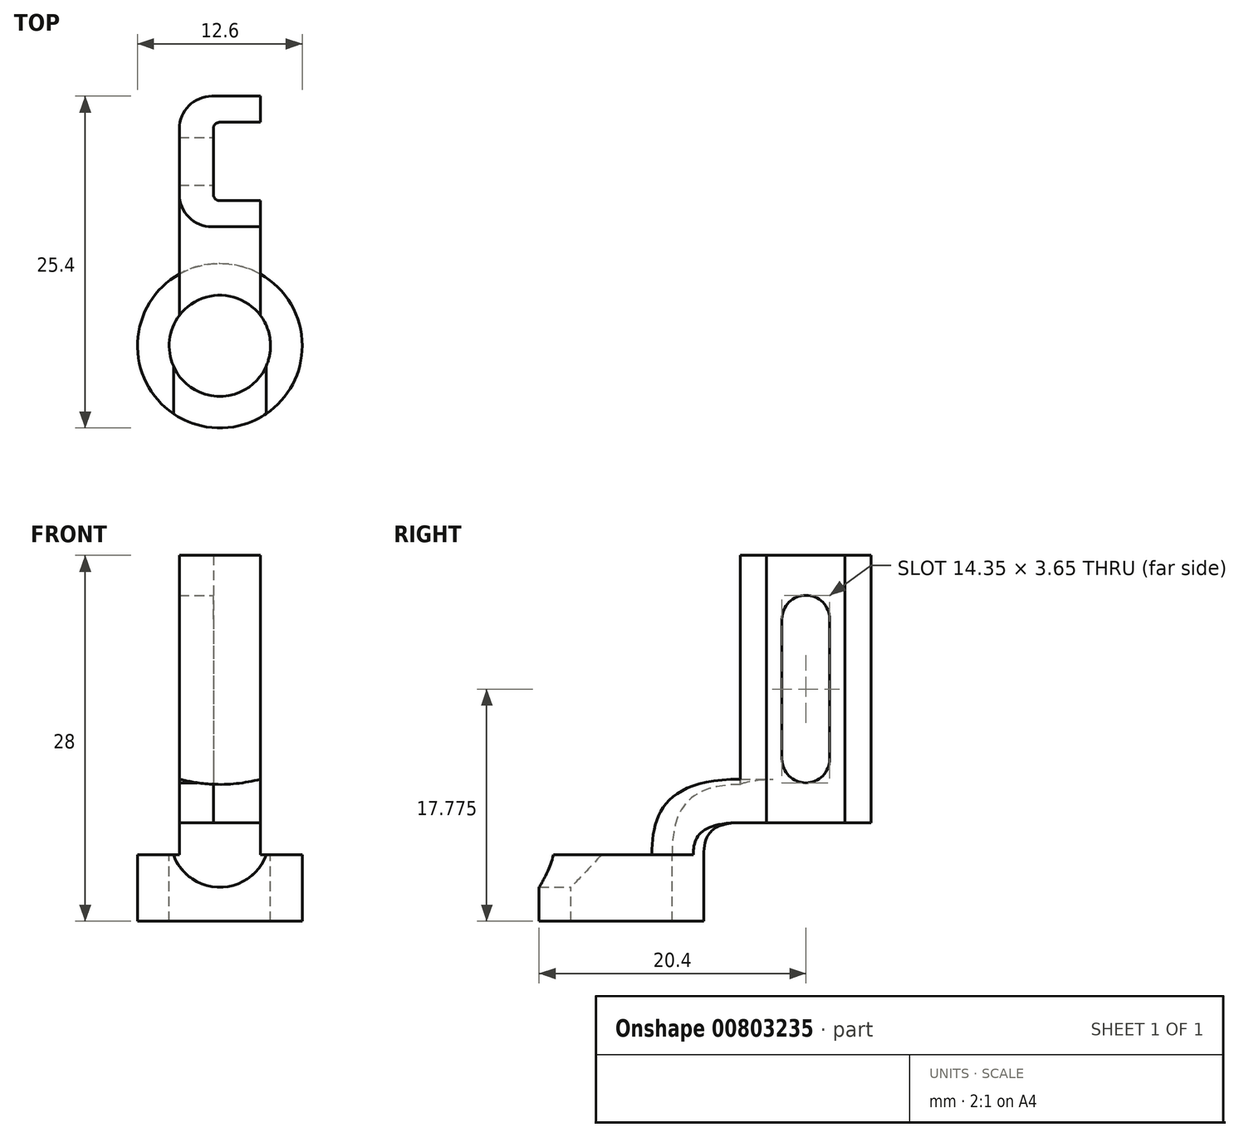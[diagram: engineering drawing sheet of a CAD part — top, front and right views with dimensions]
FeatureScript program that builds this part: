
annotation { "Feature Type Name" : "Feature", "Feature Type Description" : "" }
export const myFeature = defineFeature(function(context is Context, id is Id, definition is map)
    precondition{}
    {
        {
            var Q0;
            Q0=qCreatedBy(makeId("Top.planeOp"),FACE);
            var sketch = newSketch(context, id + "F0", { "sketchPlane" : qUnion([Q0])});
            skCircle(sketch, "E0", {"center": v(0, 0) * mm, "radius": 3.88 * mm});
            skCircle(sketch, "E1", {"center": v(0, 0) * mm, "radius": 6.3 * mm});
            skSolve(sketch);
        }
        {
            var Q0;
            Q0 = qSketchRegion(id + "F0", true);
            extrude(context, id + "F1", {"entities" : qUnion([Q0]), "oppositeDirection" : true, "depth" : 5.1 * mm, "offsetDistance" : 25 * mm});
        }
        {
            var Q0;
            Q0=makeQuery(id+"F1.opExtrude","CAP_FACE",FACE,{"disambiguationData":[OSD([sQuery(id+"F0.wireOp",EDGE,"E0"),sQuery(id+"F0.wireOp",EDGE,"E1")])],"isStart":true});
            cPlane(context, id + "F2", {"entities" : qUnion([Q0]), "cplaneType" : CPlaneType.OFFSET, "offset" : (7.55 - 5.1) * mm, "width" : 150 * mm, "height" : 150 * mm});
        }
        {
            var Q0;
            Q0=qCreatedBy(id+"F2.planeOp",FACE);
            var sketch = newSketch(context, id + "F3", { "sketchPlane" : qUnion([Q0])});
            skLineSegment(sketch, "E2.bottom", {"start": v(-3.1, 9.1) * mm, "end": v(3.1, 9.1) * mm});
            skLineSegment(sketch, "E2.top", {"start": v(-3.1, 19.1) * mm, "end": v(3.1, 19.1) * mm});
            skLineSegment(sketch, "E2.left", {"start": v(-3.1, 9.1) * mm, "end": v(-3.1, 19.1) * mm});
            skLineSegment(sketch, "E2.right", {"start": v(3.1, 9.1) * mm, "end": v(3.1, 11.1) * mm});
            skLineSegment(sketch, "E3", {"start": v(-3.1, 14.1) * mm, "end": v(3.1, 14.1) * mm, "construction": true});
            skLineSegment(sketch, "E4", {"start": v(3.1, 17.1) * mm, "end": v(-0.5, 17.1) * mm});
            skLineSegment(sketch, "E5", {"start": v(-0.5, 17.1) * mm, "end": v(-0.5, 14.1) * mm});
            skLineSegment(sketch, "E6.MirrorCS", {"start": v(3.1, 11.1) * mm, "end": v(-0.5, 11.1) * mm});
            skLineSegment(sketch, "E7.MirrorCS", {"start": v(-0.5, 11.1) * mm, "end": v(-0.5, 14.1) * mm});
            skLineSegment(sketch, "E8.trimOffspring", {"start": v(3.1, 17.1) * mm, "end": v(3.1, 19.1) * mm});
            skSolve(sketch);
        }
        {
            var Q0;
            Q0 = qSketchRegion(id + "F3", true);
            extrude(context, id + "F4", {"entities" : qUnion([Q0]), "depth" : 20.45 * mm, "offsetDistance" : 25 * mm});
        }
        {
            var Q0;
            Q0=makeQuery(id+"F4.opExtrude","SWEPT_FACE",FACE,{"disambiguationData":[OSD([sQuery(id+"F3.wireOp",EDGE,"E5"),sQuery(id+"F3.wireOp",EDGE,"E7.MirrorCS")])]});
            var sketch = newSketch(context, id + "F5", { "sketchPlane" : qUnion([Q0])});
            skLineSegment(sketch, "E9", {"start": v(11.1, 12.67) * mm, "end": v(17.1, 12.67) * mm, "construction": true});
            skLineSegment(sketch, "E10", {"start": v(14.1, 22.9) * mm, "end": v(14.1, 2.45) * mm, "construction": true});
            skArc(sketch, "E11", {"start": v(15.92, 18.02) * mm, "mid": v(14.1, 19.85) * mm, "end": v(12.27, 18.02) * mm});
            skLineSegment(sketch, "E12", {"start": v(12.27, 18.02) * mm, "end": v(12.27, 12.67) * mm});
            skLineSegment(sketch, "E13", {"start": v(15.92, 18.02) * mm, "end": v(15.92, 12.67) * mm});
            skLineSegment(sketch, "E14.MirrorCS", {"start": v(15.92, 7.32) * mm, "end": v(15.92, 12.67) * mm});
            skArc(sketch, "E15.MirrorCS", {"start": v(15.92, 7.32) * mm, "mid": v(14.1, 5.5) * mm, "end": v(12.27, 7.32) * mm});
            skLineSegment(sketch, "E16.MirrorCS", {"start": v(12.27, 7.32) * mm, "end": v(12.27, 12.67) * mm});
            skSolve(sketch);
        }
        {
            var Q0;
            Q0 = qSketchRegion(id + "F5", true);
            extrude(context, id + "F6", {"entities" : qUnion([Q0]), "operationType" : NewBodyOperationType.REMOVE, "endBound" : BoundingType.UP_TO_NEXT, "oppositeDirection" : true, "depth" : 25 * mm, "offsetDistance" : 25 * mm});
        }
        {
            var Q0;
            Q0=makeQuery(id+"F4.opExtrude","SWEPT_FACE",FACE,{"disambiguationData":[OSD([sQuery(id+"F3.wireOp",EDGE,"E2.bottom")])]});
            var sketch = newSketch(context, id + "F7", { "sketchPlane" : qUnion([Q0])});
            skLineSegment(sketch, "E17.bottom", {"start": v(3.1, 5.78) * mm, "end": v(-3.1, 5.78) * mm});
            skLineSegment(sketch, "E17.left", {"start": v(3.1, -6.22) * mm, "end": v(3.1, 5.78) * mm});
            skLineSegment(sketch, "E17.right", {"start": v(-3.1, -6.22) * mm, "end": v(-3.1, 5.78) * mm});
            skPoint(sketch, "E18.centerSnap0", {"position": v(0, -6.22) * mm});
            skLineSegment(sketch, "E19", {"start": v(-3.1, -6.22) * mm, "end": v(3.1, -6.22) * mm});
            skSolve(sketch);
        }
        {
            var Q0;
            Q0=makeQuery(id+"F1.opExtrude","CAP_FACE",FACE,{"disambiguationData":[OSD([sQuery(id+"F0.wireOp",EDGE,"E0"),sQuery(id+"F0.wireOp",EDGE,"E1")])],"isStart":true});
            var sketch = newSketch(context, id + "F8", { "sketchPlane" : qUnion([Q0])});
            skCircle(sketch, "E20.0", {"center": v(0, 0) * mm, "radius": 3.88 * mm});
            skSolve(sketch);
        }
        {
            var Q0;
            {var subQ0=sQuery(id+"F7.wireOp",EDGE,"E17.bottom");Q0=makeQuery(id+"F7.imprint","IMPRINT",FACE,{"disambiguationData":[TD([[makeQuery(id+"F7.imprint","IMPRINT",EDGE,{"derivedFrom":subQ0}),-1.0]])]});}
            var sketch = newSketch(context, id + "F9", { "sketchPlane" : qUnion([Q0])});
            skLineSegment(sketch, "E21.bottom", {"start": v(3.1, 2.45) * mm, "end": v(-3.1, 2.45) * mm});
            skLineSegment(sketch, "E21.top", {"start": v(3.1, 5.78) * mm, "end": v(-3.1, 5.78) * mm, "construction": true});
            skLineSegment(sketch, "E21.left", {"start": v(3.1, 2.45) * mm, "end": v(3.1, 5.78) * mm});
            skLineSegment(sketch, "E21.right", {"start": v(-3.1, 2.45) * mm, "end": v(-3.1, 5.78) * mm});
            skArc(sketch, "E22", {"start": v(-3.1, 5.78) * mm, "mid": v(0, 5.37) * mm, "end": v(3.1, 5.78) * mm});
            skSolve(sketch);
        }
        {
            var Q0;
            Q0=makeQuery(id+"F8.imprint","IMPRINT",FACE,{"disambiguationData":[TD([[makeQuery(id+"F8.imprint","IMPRINT",EDGE,{"derivedFrom":sQuery(id+"F8.wireOp",EDGE,"E20.0")}),-1.0]])]});
            var sketch = newSketch(context, id + "F10", { "sketchPlane" : qUnion([Q0])});
            skArc(sketch, "E23.0", {"start": v(3.1, 5.48) * mm, "mid": v(0, 6.3) * mm, "end": v(-3.1, 5.48) * mm});
            skArc(sketch, "E24.0", {"start": v(3.1, 2.33) * mm, "mid": v(0, 3.88) * mm, "end": v(-3.1, 2.33) * mm});
            skLineSegment(sketch, "E25", {"start": v(-3.1, 5.48) * mm, "end": v(-3.1, 2.33) * mm});
            skLineSegment(sketch, "E26", {"start": v(0, 0) * mm, "end": v(0, 6.3) * mm, "construction": true});
            skLineSegment(sketch, "E27.MirrorCS", {"start": v(3.1, 5.48) * mm, "end": v(3.1, 2.33) * mm});
            skSolve(sketch);
        }
        {
            var Q0;
            Q0=qCreatedBy(makeId("Right.planeOp"),FACE);
            var sketch = newSketch(context, id + "F11", { "sketchPlane" : qUnion([Q0])});
            skLineSegment(sketch, "E28", {"start": v(3.88, 0) * mm, "end": v(3.88, 1) * mm, "construction": true});
            skEllipticalArc(sketch, "E29", {});
            skLineSegment(sketch, "E30", {"start": v(9.1, 5.37) * mm, "end": v(9.1, -5.37) * mm, "construction": true});
            const initialGuessF11  = {"E29": [0.0091, 0, -1, 0, 0.005225, 0.010422670097954136, 4.71238898038469, 6.283185307179586]};
            skSetInitialGuess(sketch, initialGuessF11);
            skSolve(sketch);
        }
        {
            var Q2;
            Q2=makeQuery(id+"F10.imprint","IMPRINT",FACE,{"disambiguationData":[TD([[makeQuery(id+"F10.imprint","IMPRINT",EDGE,{"derivedFrom":sQuery(id+"F10.wireOp",EDGE,"E23.0")}),1.0]])]});
            var Q3;
            Q3=makeQuery(id+"F9.imprint","IMPRINT",FACE,{"disambiguationData":[TD([[makeQuery(id+"F9.imprint","IMPRINT",EDGE,{"derivedFrom":sQuery(id+"F9.wireOp",EDGE,"E21.bottom")}),-1.0]])]});
            var Q4;
            Q4=sQuery(id+"F11.wireOp",EDGE,"E29");
            var Q5;
            Q5=sQuery(id+"F10.wireOp",VERTEX,"E23.0.end");
            var Q6;
            Q6=sQuery(id+"F9.wireOp",VERTEX,"E21.bottom.end");
            loft(context, id + "F12", {"operationType" : NewBodyOperationType.ADD, "startCondition" : LoftEndDerivativeType.NORMAL_TO_PROFILE, "startMagnitude" : 1.5, "endCondition" : LoftEndDerivativeType.NORMAL_TO_PROFILE, "endMagnitude" : 2.5, "sheetProfilesArray" : [{ "sheetProfileEntities" : qUnion([Q2]) }, { "sheetProfileEntities" : qUnion([Q3]) }], "guidesArray" : [{ "guideEntities" : qUnion([Q4]), "guideDerivativeType" : LoftGuideDerivativeType.DEFAULT, "guideDerivativeMagnitude" : 1 }], "connections" : [{ "connectionEntities" : qUnion([Q5, Q6]), "connectionEdgeQueries" : qUnion([]), "connectionEdgeParameters" : [] }]});
        }
        {
            var Q0;
            Q0=qCreatedBy(makeId("Right.planeOp"),FACE);
            var sketch = newSketch(context, id + "F13", { "sketchPlane" : qUnion([Q0])});
            skLineSegment(sketch, "E31", {"start": v(6.3, -0.55) * mm, "end": v(6.3, -5.1) * mm});
            skLineSegment(sketch, "E32", {"start": v(12.3, 2.45) * mm, "end": v(9.3, 2.45) * mm});
            skLineSegment(sketch, "E33", {"start": v(12.3, 2.45) * mm, "end": v(12.3, -5.1) * mm});
            skLineSegment(sketch, "E34", {"start": v(12.3, -5.1) * mm, "end": v(6.3, -5.1) * mm});
            skPoint(sketch, "E35.visualSharp", {"position": v(6.3, 2.45) * mm});
            skArc(sketch, "E35.filletArc", {"start": v(9.3, 2.45) * mm, "mid": v(7.18, 1.57) * mm, "end": v(6.3, -0.55) * mm});
            skSolve(sketch);
        }
        {
            var Q0;
            Q0=makeQuery(id+"F4.opExtrude","SWEPT_EDGE",EDGE,{"disambiguationData":[OSD([sQuery(id+"F3.wireOp",EDGE,"E6.MirrorCS"),sQuery(id+"F3.wireOp",EDGE,"E7.MirrorCS")])]});
            var Q1;
            Q1=makeQuery(id+"F4.opExtrude","SWEPT_EDGE",EDGE,{"disambiguationData":[OSD([sQuery(id+"F3.wireOp",EDGE,"E4"),sQuery(id+"F3.wireOp",EDGE,"E5")])]});
            fillet(context, id + "F14", {"entities" : qUnion([Q0, Q1]), "radius" : 0.5 * mm, "tangentPropagation" : true, "allowEdgeOverflow" : false});
        }
        {
            var Q0;
            Q0=makeQuery(id+"F4.opExtrude","SWEPT_EDGE",EDGE,{"disambiguationData":[OSD([sQuery(id+"F3.wireOp",EDGE,"E2.bottom"),sQuery(id+"F3.wireOp",EDGE,"E2.left")])]});
            var Q1;
            Q1=makeQuery(id+"F4.opExtrude","SWEPT_EDGE",EDGE,{"disambiguationData":[OSD([sQuery(id+"F3.wireOp",EDGE,"E2.top"),sQuery(id+"F3.wireOp",EDGE,"E2.left")])]});
            fillet(context, id + "F15", {"entities" : qUnion([Q0, Q1]), "radius" : 2.5 * mm, "tangentPropagation" : true, "allowEdgeOverflow" : false});
        }
        {
            var Q0;
            Q0=qCreatedBy(makeId("Front.planeOp"),FACE);
            var sketch = newSketch(context, id + "F16", { "sketchPlane" : qUnion([Q0])});
            skArc(sketch, "E36", {"start": v(-3.55, 0) * mm, "mid": v(0, -2.5) * mm, "end": v(3.55, 0) * mm});
            skLineSegment(sketch, "E37", {"start": v(-3.55, 0) * mm, "end": v(-3.55, -5.1) * mm, "construction": true});
            skLineSegment(sketch, "E38", {"start": v(3.55, 0) * mm, "end": v(3.55, -5.1) * mm, "construction": true});
            skLineSegment(sketch, "E39", {"start": v(0, 0) * mm, "end": v(0, 1.27) * mm, "construction": true});
            skLineSegment(sketch, "E40", {"start": v(-3.55, 0) * mm, "end": v(3.55, 0) * mm});
            skSolve(sketch);
        }
        {
            var Q0;
            Q0 = qSketchRegion(id + "F16", true);
            extrude(context, id + "F17", {"entities" : qUnion([Q0]), "operationType" : NewBodyOperationType.REMOVE, "endBound" : BoundingType.THROUGH_ALL, "depth" : 25 * mm, "offsetDistance" : 25 * mm});
        }
    });
